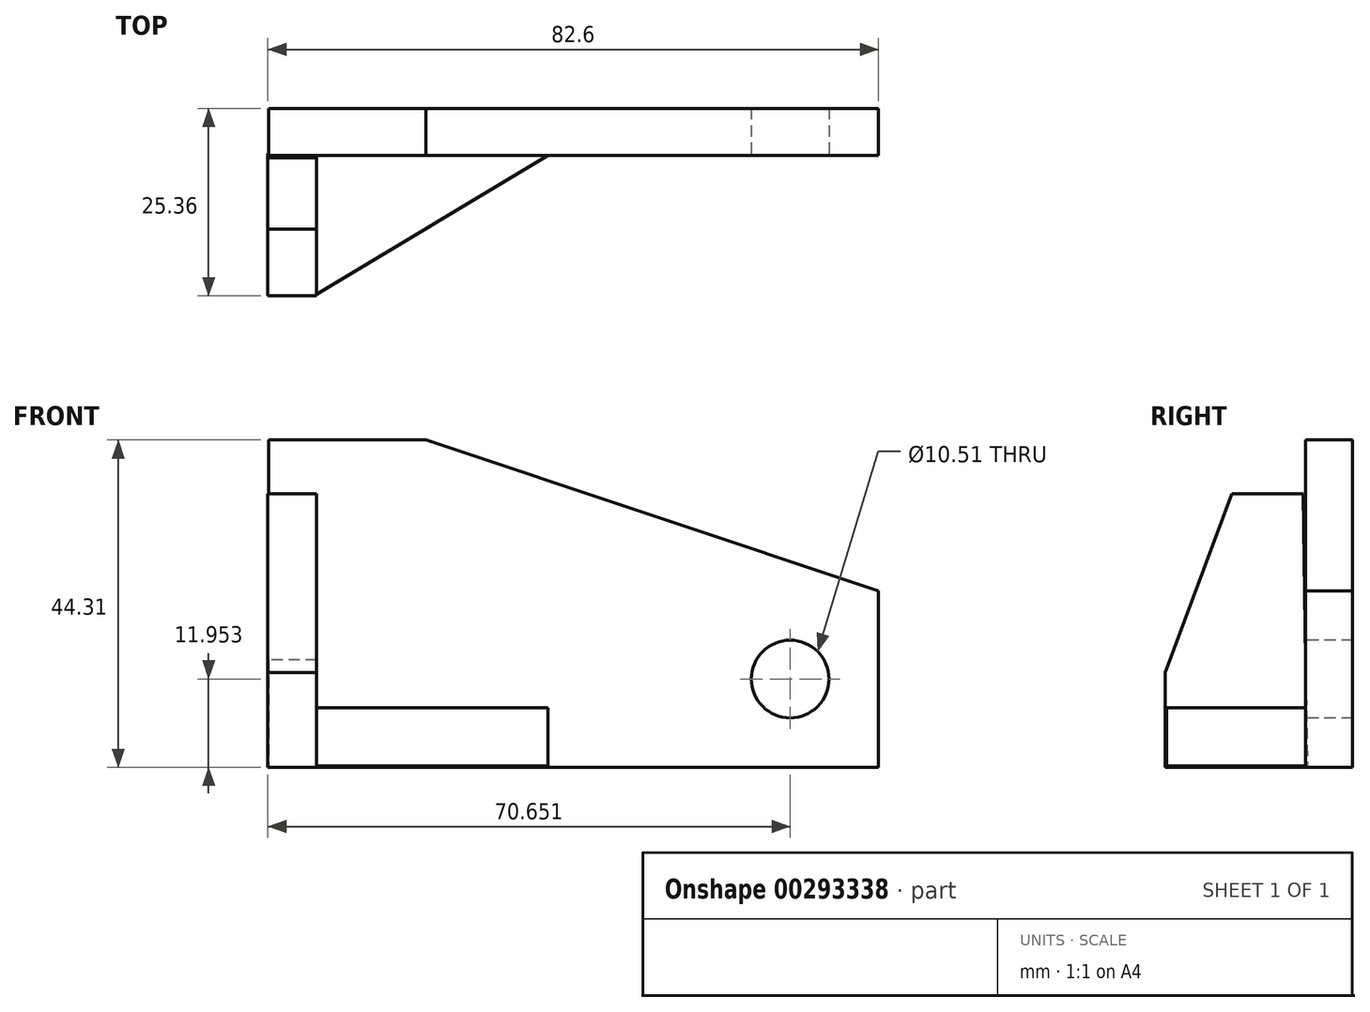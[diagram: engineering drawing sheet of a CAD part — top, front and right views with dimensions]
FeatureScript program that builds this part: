
annotation { "Feature Type Name" : "Feature", "Feature Type Description" : "" }
export const myFeature = defineFeature(function(context is Context, id is Id, definition is map)
    precondition{}
    {
        {
            var Q0;
            Q0=qCreatedBy(makeId("Front.planeOp"),FACE);
            var sketch = newSketch(context, id + "F0", { "sketchPlane" : qUnion([Q0])});
            skLineSegment(sketch, "E0", {"start": v(-52.47, 40.08) * mm, "end": v(-31.19, 40.08) * mm});
            skLineSegment(sketch, "E1", {"start": v(-31.19, 40.08) * mm, "end": v(30.02, 19.67) * mm});
            skLineSegment(sketch, "E2", {"start": v(30.02, 19.67) * mm, "end": v(30.02, -4.23) * mm});
            skLineSegment(sketch, "E3", {"start": v(30.02, -4.23) * mm, "end": v(-52.47, -4.23) * mm});
            skLineSegment(sketch, "E4", {"start": v(-52.47, -4.23) * mm, "end": v(-52.47, 40.08) * mm});
            skSolve(sketch);
        }
        {
            var Q0;
            Q0 = qSketchRegion(id + "F0", true);
            extrude(context, id + "F1", {"entities" : qUnion([Q0]), "depth" : 6.35 * mm});
        }
        {
            var Q0;
            Q0=qCreatedBy(makeId("Right.planeOp"),FACE);
            var sketch = newSketch(context, id + "F2", { "sketchPlane" : qUnion([Q0])});
            skLineSegment(sketch, "E5", {"start": v(-6.7, 32.8) * mm, "end": v(-16.32, 32.8) * mm});
            skLineSegment(sketch, "E6", {"start": v(-16.32, 32.8) * mm, "end": v(-25.36, 8.6) * mm});
            skLineSegment(sketch, "E7", {"start": v(-25.36, 8.6) * mm, "end": v(-25.36, -4.23) * mm});
            skLineSegment(sketch, "E8", {"start": v(-25.36, -4.23) * mm, "end": v(-6.12, -4.23) * mm});
            skLineSegment(sketch, "E9", {"start": v(-6.12, -4.23) * mm, "end": v(-6.7, 32.8) * mm});
            skSolve(sketch);
        }
        {
            var Q0;
            Q0 = qSketchRegion(id + "F2", true);
            extrude(context, id + "F3", {"entities" : qUnion([Q0]), "operationType" : NewBodyOperationType.ADD, "oppositeDirection" : true, "depth" : 52.58 * mm});
        }
        {
            var Q0;
            Q0=makeQuery(id+"F3.opExtrude","CAP_FACE",FACE,{"disambiguationData":[OSD([sQuery(id+"F2.wireOp",EDGE,"E5"),sQuery(id+"F2.wireOp",EDGE,"E6"),sQuery(id+"F2.wireOp",EDGE,"E7"),sQuery(id+"F2.wireOp",EDGE,"E8"),sQuery(id+"F2.wireOp",EDGE,"E9")])],"isStart":true});
            extrude(context, id + "F4", {"entities" : qUnion([Q0]), "operationType" : NewBodyOperationType.REMOVE, "oppositeDirection" : true, "depth" : 45.97 * mm});
        }
        {
            var Q0;
            Q0=qCreatedBy(makeId("Top.planeOp"),FACE);
            var sketch = newSketch(context, id + "F5", { "sketchPlane" : qUnion([Q0])});
            skLineSegment(sketch, "E10", {"start": v(-46.05, -25.21) * mm, "end": v(-46.05, -6.27) * mm});
            skLineSegment(sketch, "E11", {"start": v(-46.05, -6.27) * mm, "end": v(-14.57, -6.27) * mm});
            skLineSegment(sketch, "E12", {"start": v(-14.57, -6.27) * mm, "end": v(-46.05, -25.21) * mm});
            skSolve(sketch);
        }
        {
            var Q0;
            Q0 = qSketchRegion(id + "F5", true);
            extrude(context, id + "F6", {"entities" : qUnion([Q0]), "operationType" : NewBodyOperationType.ADD, "oppositeDirection" : true, "depth" : 4.06 * mm});
        }
        {
            var Q0;
            Q0=makeQuery(id+"F6.opExtrude","CAP_FACE",FACE,{"disambiguationData":[OSD([sQuery(id+"F5.wireOp",EDGE,"E10"),sQuery(id+"F5.wireOp",EDGE,"E11"),sQuery(id+"F5.wireOp",EDGE,"E12")])],"isStart":true});
            extrude(context, id + "F7", {"entities" : qUnion([Q0]), "operationType" : NewBodyOperationType.ADD, "depth" : 3.8 * mm});
        }
        {
            var Q0;
            {var subQ0=sQuery(id+"F0.wireOp",EDGE,"E4");var subQ1=sQuery(id+"F0.wireOp",EDGE,"E3");var subQ2=sQuery(id+"F0.wireOp",EDGE,"E2");var subQ3=sQuery(id+"F0.wireOp",EDGE,"E1");var subQ4=sQuery(id+"F0.wireOp",EDGE,"E0");Q0=makeQuery(id+"F4.boolean.opBoolean","MERGE",FACE,{"derivedFrom":[makeQuery(id+"F1.opExtrude","CAP_FACE",FACE,{"disambiguationData":[OSD([subQ4,subQ3,subQ2,subQ1,subQ0])],"isStart":false}),makeQuery(id+"F4.opExtrude","SWEPT_FACE",FACE,{"disambiguationData":[OSD([subQ4,subQ3,subQ2,subQ1,subQ0,sQuery(id+"F2.wireOp",EDGE,"E5"),sQuery(id+"F2.wireOp",EDGE,"E6"),sQuery(id+"F2.wireOp",EDGE,"E7"),sQuery(id+"F2.wireOp",EDGE,"E8"),sQuery(id+"F2.wireOp",EDGE,"E9")])]})]});}
            var sketch = newSketch(context, id + "F8", { "sketchPlane" : qUnion([Q0])});
            skCircle(sketch, "E13", {"center": v(18.07, 7.72) * mm, "radius": 5.25 * mm});
            skPoint(sketch, "E13.centerSnap0", {"position": v(30.02, 7.72) * mm});
            skSolve(sketch);
        }
        {
            var Q0;
            Q0 = qSketchRegion(id + "F8", true);
            extrude(context, id + "F9", {"entities" : qUnion([Q0]), "operationType" : NewBodyOperationType.REMOVE, "oppositeDirection" : true, "depth" : 25.4 * mm});
        }
    });
